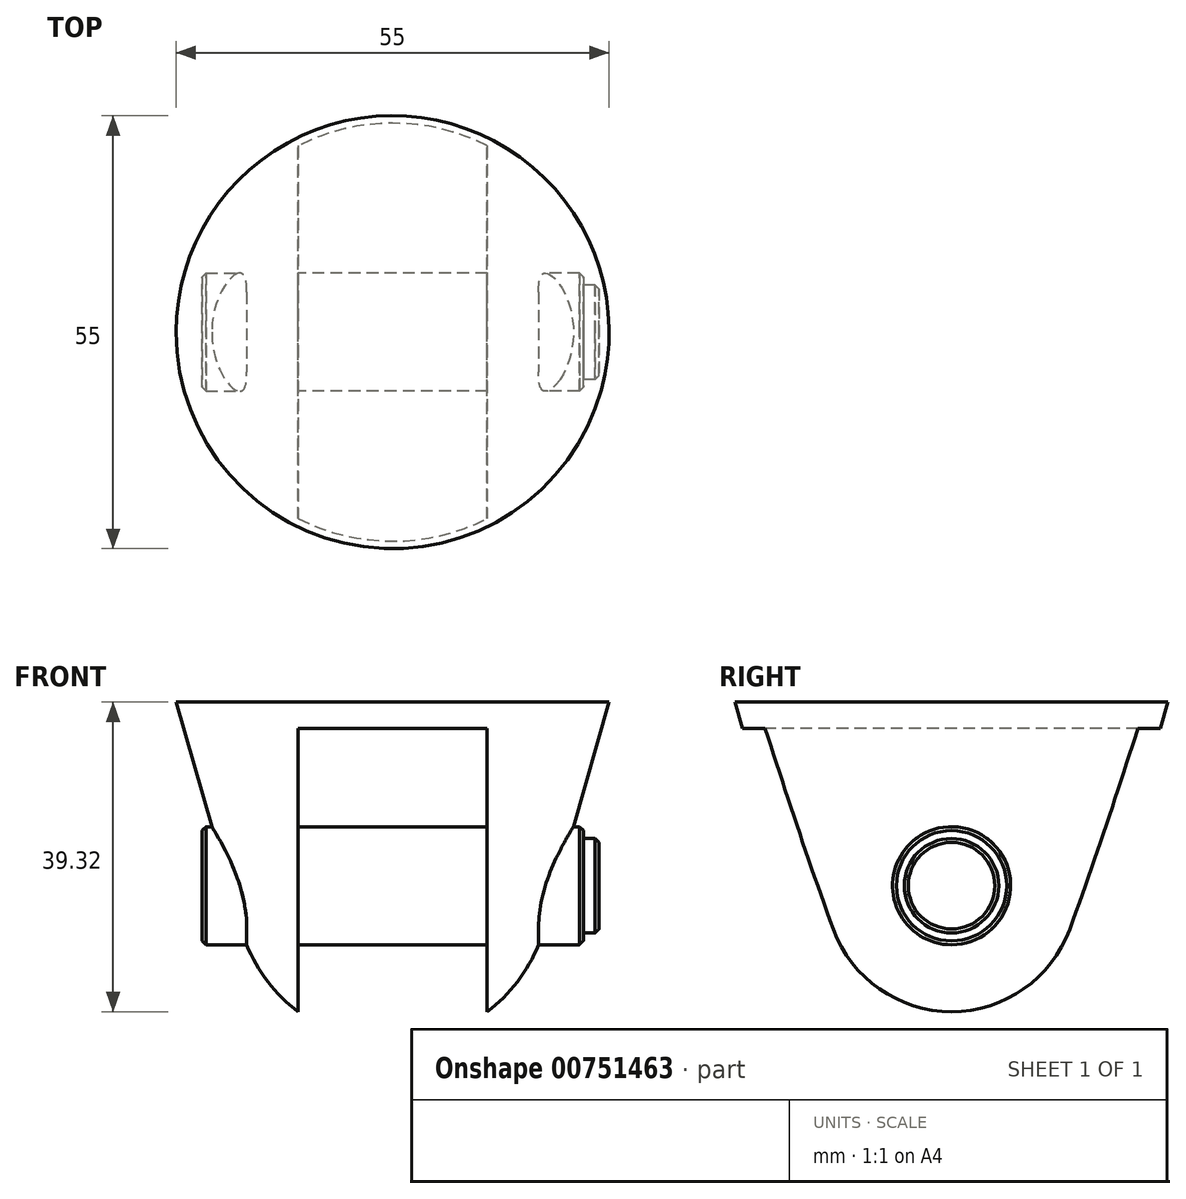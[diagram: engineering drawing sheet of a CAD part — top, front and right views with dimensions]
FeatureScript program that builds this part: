
annotation { "Feature Type Name" : "Feature", "Feature Type Description" : "" }
export const myFeature = defineFeature(function(context is Context, id is Id, definition is map)
    precondition{}
    {
        {
            var Q0;
            Q0=qCreatedBy(makeId("Front.planeOp"),FACE);
            var sketch = newSketch(context, id + "F0", { "sketchPlane" : qUnion([Q0])});
            skLineSegment(sketch, "E0", {"start": v(0, 0) * mm, "end": v(27.5, 0) * mm});
            skLineSegment(sketch, "E1", {"start": v(27.5, 0) * mm, "end": v(19.22, -28.84) * mm});
            skArc(sketch, "E2", {"start": v(0, -43.32) * mm, "mid": v(12.03, -39.3) * mm, "end": v(19.22, -28.84) * mm});
            skLineSegment(sketch, "E3", {"start": v(0, 0) * mm, "end": v(0, -43.32) * mm});
            skLineSegment(sketch, "E4", {"start": v(0, 0) * mm, "end": v(0, 8.72) * mm, "construction": true});
            skLineSegment(sketch, "E5", {"start": v(0, -23.32) * mm, "end": v(19.22, -28.84) * mm, "construction": true});
            skArc(sketch, "E6", {"start": v(19.22, -28.84) * mm, "mid": v(15.97, -11.28) * mm, "end": v(0, -3.32) * mm, "construction": true});
            skLineSegment(sketch, "E7", {"start": v(0, -3.32) * mm, "end": v(26.55, -3.32) * mm, "construction": true});
            skLineSegment(sketch, "E8", {"start": v(12, -3.32) * mm, "end": v(12, -43.32) * mm, "construction": true});
            skLineSegment(sketch, "E9", {"start": v(12, -43.32) * mm, "end": v(0, -43.32) * mm, "construction": true});
            skCircle(sketch, "E10", {"center": v(0, -23.32) * mm, "radius": 20 * mm, "construction": true});
            skSolve(sketch);
        }
        {
            var Q0;
            Q0=qSketchRegion(id+"F0",true);
            var Q1;
            Q1=sQuery(id+"F0.wireOp",EDGE,"E4");
            revolve(context, id + "F1", {"surfaceOperationType" : NewSurfaceOperationType.NEW, "entities" : qUnion([Q0]), "axis" : qUnion([Q1]), "revolveType" : RevolveType.FULL});
        }
        {
            var Q0;
            Q0=qCreatedBy(makeId("Front.planeOp"),FACE);
            var sketch = newSketch(context, id + "F2", { "sketchPlane" : qUnion([Q0])});
            skLineSegment(sketch, "E11", {"start": v(12, -43.32) * mm, "end": v(12, -3.32) * mm});
            skLineSegment(sketch, "E12", {"start": v(12, -3.32) * mm, "end": v(0, -3.32) * mm});
            skLineSegment(sketch, "E13", {"start": v(0, -3.32) * mm, "end": v(0, -43.32) * mm, "construction": true});
            skLineSegment(sketch, "E14", {"start": v(0, -43.32) * mm, "end": v(12, -43.32) * mm});
            skLineSegment(sketch, "E15.MirrorCS", {"start": v(0, -43.32) * mm, "end": v(-12, -43.32) * mm});
            skLineSegment(sketch, "E16.MirrorCS", {"start": v(-12, -43.32) * mm, "end": v(-12, -3.32) * mm});
            skLineSegment(sketch, "E17.MirrorCS", {"start": v(-12, -3.32) * mm, "end": v(0, -3.32) * mm});
            skSolve(sketch);
        }
        {
            var Q0;
            Q0=qSketchRegion(id+"F2",true);
            extrude(context, id + "F3", {"entities" : qUnion([Q0]), "operationType" : NewBodyOperationType.REMOVE, "endBound" : BoundingType.THROUGH_ALL, "oppositeDirection" : true, "depth" : 25 * mm, "offsetDistance" : 25 * mm, "hasSecondDirection" : true, "secondDirectionBound" : SecondDirectionBoundingType.THROUGH_ALL, "secondDirectionOppositeDirection" : false, "secondDirectionDepth" : 25 * mm});
        }
        {
            var Q0;
            Q0=qCreatedBy(makeId("Right.planeOp"),FACE);
            var sketch = newSketch(context, id + "F4", { "sketchPlane" : qUnion([Q0])});
            skCircle(sketch, "E18", {"center": v(0, -23.32) * mm, "radius": 7.5 * mm});
            skSolve(sketch);
        }
        {
            var Q0;
            Q0=qSketchRegion(id+"F4",true);
            var Q1;
            Q1=sQuery(id+"F0.wireOp",VERTEX,"E1.end");
            extrude(context, id + "F5", {"entities" : qUnion([Q0]), "operationType" : NewBodyOperationType.ADD, "endBound" : BoundingType.UP_TO_VERTEX, "depth" : 25 * mm, "endBoundEntityVertex" : qUnion([Q1]), "hasOffset" : true, "offsetDistance" : 5 * mm, "offsetOppositeDirection" : true});
        }
        {
            var Q0;
            Q0=makeQuery(id+"F1.opRevolve","SWEPT_BODY",BODY,{"disambiguationData":[OSD([sQuery(id+"F0.wireOp",EDGE,"E0"),sQuery(id+"F0.wireOp",EDGE,"E1"),sQuery(id+"F0.wireOp",EDGE,"E2"),sQuery(id+"F0.wireOp",EDGE,"E3")])]});
            var Q1;
            Q1=qCreatedBy(makeId("Right.planeOp"),FACE);
            mirror(context, id + "F6", {"operationType" : NewBodyOperationType.ADD, "entities" : qUnion([Q0]), "mirrorPlane" : qUnion([Q1])});
        }
        {
            var Q0;
            Q0=makeQuery(id+"F5.opExtrude","CAP_FACE",FACE,{"disambiguationData":[OSD([sQuery(id+"F4.wireOp",EDGE,"E18")])],"isStart":false});
            var sketch = newSketch(context, id + "F7", { "sketchPlane" : qUnion([Q0])});
            skCircle(sketch, "E19", {"center": v(0, -23.32) * mm, "radius": 6 * mm});
            skSolve(sketch);
        }
        {
            var Q0;
            Q0=qSketchRegion(id+"F7",true);
            var Q1;
            Q1=makeQuery(id+"F3.boolean.opBoolean","COPY",FACE,{"derivedFrom":makeQuery(id+"F3.opExtrude","SWEPT_FACE",FACE,{"disambiguationData":[OSD([sQuery(id+"F2.wireOp",EDGE,"E11")])]})});
            var Q2;
            Q2=makeQuery(id+"F1.opRevolve","SWEPT_BODY",BODY,{"disambiguationData":[OSD([sQuery(id+"F0.wireOp",EDGE,"E0"),sQuery(id+"F0.wireOp",EDGE,"E1"),sQuery(id+"F0.wireOp",EDGE,"E2"),sQuery(id+"F0.wireOp",EDGE,"E3")])]});
            extrude(context, id + "F8", {"entities" : qUnion([Q0]), "operationType" : NewBodyOperationType.ADD, "depth" : 2 * mm, "offsetDistance" : 25 * mm, "hasSecondDirection" : true, "secondDirectionBound" : SecondDirectionBoundingType.UP_TO_SURFACE, "secondDirectionOppositeDirection" : true, "secondDirectionDepth" : 25 * mm, "secondDirectionBoundEntityFace" : qUnion([Q1]), "secondDirectionBoundEntityBody" : qUnion([Q2])});
        }
        {
            var Q0;
            Q0=makeQuery(id+"F8.opExtrude","CAP_EDGE",EDGE,{"disambiguationData":[OSD([sQuery(id+"F7.wireOp",EDGE,"E19")])],"isStart":false});
            var Q1;
            Q1=makeQuery(id+"F6.opPattern","COPY",EDGE,{"derivedFrom":makeQuery(id+"F5.opExtrude","CAP_EDGE",EDGE,{"disambiguationData":[OSD([sQuery(id+"F4.wireOp",EDGE,"E18")])],"isStart":false}),"instanceName":"1"});
            var Q2;
            Q2=makeQuery(id+"F5.opExtrude","CAP_EDGE",EDGE,{"disambiguationData":[OSD([sQuery(id+"F4.wireOp",EDGE,"E18")])],"isStart":false});
            chamfer(context, id + "F9", {"entities" : qUnion([Q0, Q1, Q2]), "width" : 0.5 * mm, "tangentPropagation" : true});
        }
    });
